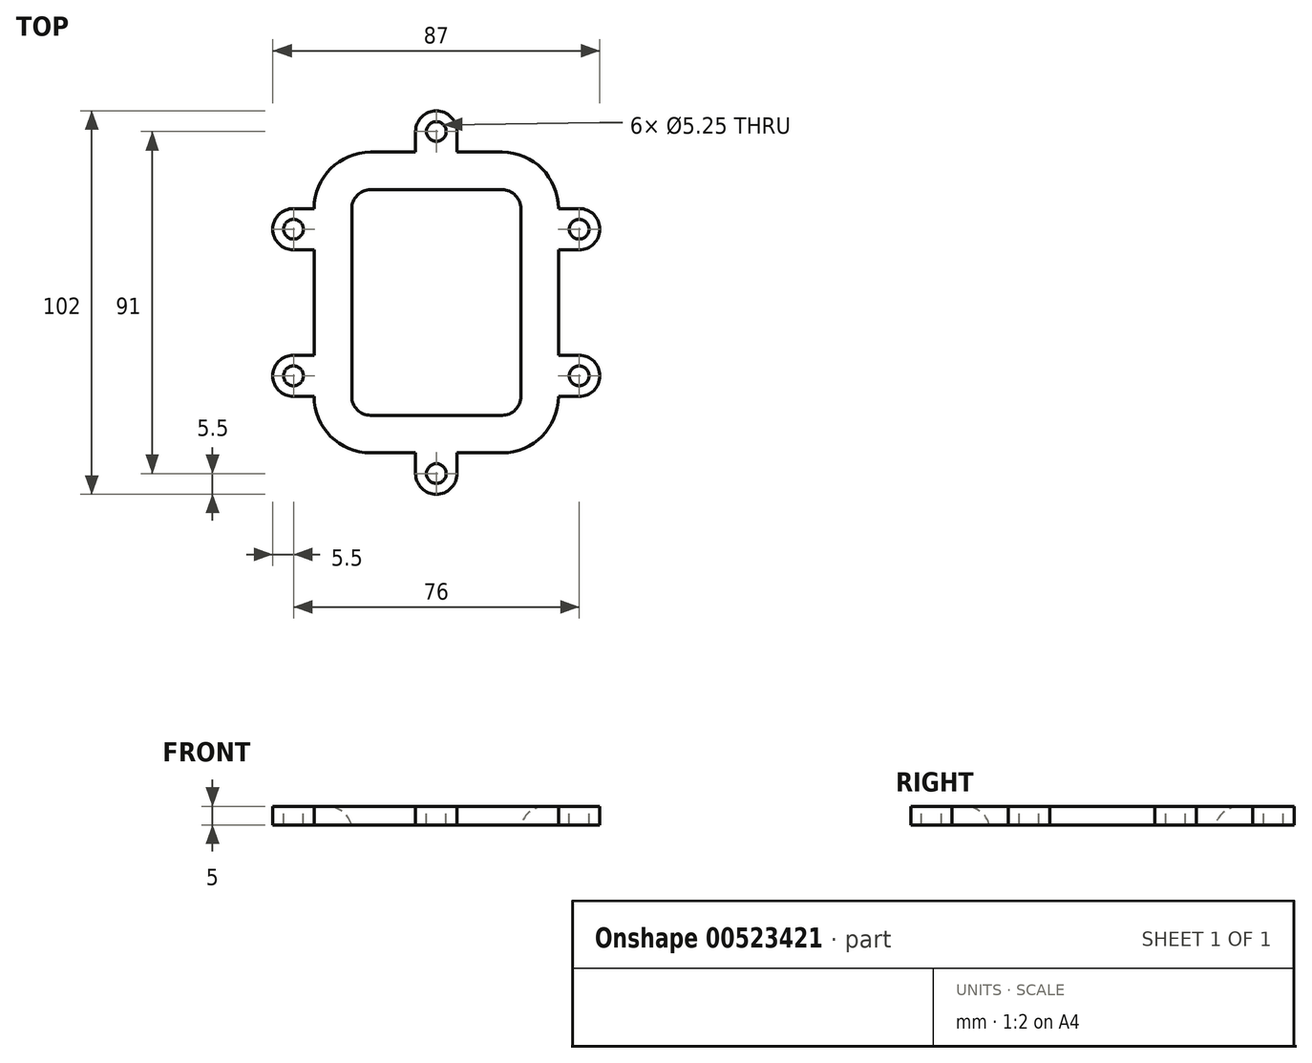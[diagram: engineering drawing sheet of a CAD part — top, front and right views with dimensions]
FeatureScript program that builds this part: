
annotation { "Feature Type Name" : "Feature", "Feature Type Description" : "" }
export const myFeature = defineFeature(function(context is Context, id is Id, definition is map)
    precondition{}
    {
        {
            var Q0;
            Q0=qCreatedBy(makeId("Top.planeOp"),FACE);
            var sketch = newSketch(context, id + "F0", { "sketchPlane" : qUnion([Q0])});
            skLineSegment(sketch, "E0.bottom", {"start": v(-17.5, -30) * mm, "end": v(17.5, -30) * mm});
            skLineSegment(sketch, "E0.top", {"start": v(-17.5, 30) * mm, "end": v(17.5, 30) * mm});
            skLineSegment(sketch, "E0.left", {"start": v(-22.5, -25) * mm, "end": v(-22.5, 25) * mm});
            skLineSegment(sketch, "E0.right", {"start": v(22.5, -25) * mm, "end": v(22.5, 25) * mm});
            skPoint(sketch, "E0.middle", {"position": v(0, 0) * mm});
            skPoint(sketch, "E1.visualSharp", {"position": v(22.5, -30) * mm});
            skArc(sketch, "E1.filletArc", {"start": v(17.5, -30) * mm, "mid": v(21.04, -28.54) * mm, "end": v(22.5, -25) * mm});
            skPoint(sketch, "E2.visualSharp", {"position": v(-22.5, -30) * mm});
            skArc(sketch, "E2.filletArc", {"start": v(-22.5, -25) * mm, "mid": v(-21.04, -28.54) * mm, "end": v(-17.5, -30) * mm});
            skPoint(sketch, "E3.visualSharp", {"position": v(-22.5, 30) * mm});
            skArc(sketch, "E3.filletArc", {"start": v(-17.5, 30) * mm, "mid": v(-21.04, 28.54) * mm, "end": v(-22.5, 25) * mm});
            skPoint(sketch, "E4.visualSharp", {"position": v(22.5, 30) * mm});
            skArc(sketch, "E4.filletArc", {"start": v(22.5, 25) * mm, "mid": v(21.04, 28.54) * mm, "end": v(17.5, 30) * mm});
            skArc(sketch, "E5.0", {"start": v(-32.5, -25) * mm, "mid": v(-28.1, -35.6) * mm, "end": v(-17.5, -40) * mm});
            skLineSegment(sketch, "E5.1", {"start": v(-17.5, -40) * mm, "end": v(-5.5, -40) * mm});
            skLineSegment(sketch, "E5.2", {"start": v(-32.5, -14) * mm, "end": v(-32.5, 14) * mm});
            skArc(sketch, "E5.3", {"start": v(17.5, -40) * mm, "mid": v(28.1, -35.6) * mm, "end": v(32.5, -25) * mm});
            skArc(sketch, "E5.4", {"start": v(-17.5, 40) * mm, "mid": v(-28.1, 35.6) * mm, "end": v(-32.5, 25) * mm});
            skLineSegment(sketch, "E5.5", {"start": v(-17.5, 40) * mm, "end": v(-5.5, 40) * mm});
            skArc(sketch, "E5.6", {"start": v(32.5, 25) * mm, "mid": v(28.1, 35.6) * mm, "end": v(17.5, 40) * mm});
            skLineSegment(sketch, "E5.7", {"start": v(32.5, -14) * mm, "end": v(32.5, 14) * mm});
            skArc(sketch, "E6", {"start": v(-38, 25) * mm, "mid": v(-43.5, 19.5) * mm, "end": v(-38, 14) * mm});
            skLineSegment(sketch, "E7", {"start": v(-38, 25) * mm, "end": v(-32.5, 25) * mm});
            skLineSegment(sketch, "E8", {"start": v(-38, 14) * mm, "end": v(-32.5, 14) * mm});
            skCircle(sketch, "E9", {"center": v(-38, 19.5) * mm, "radius": 2.5 * mm, "construction": true});
            skLineSegment(sketch, "E10", {"start": v(0, 49.94) * mm, "end": v(0, -61.1) * mm, "construction": true});
            skLineSegment(sketch, "E11", {"start": v(-88.08, 0) * mm, "end": v(87.86, 0) * mm, "construction": true});
            skLineSegment(sketch, "E12.MirrorCS", {"start": v(38, 25) * mm, "end": v(32.5, 25) * mm});
            skLineSegment(sketch, "E13.MirrorCS", {"start": v(38, 14) * mm, "end": v(32.5, 14) * mm});
            skArc(sketch, "E14.MirrorCS", {"start": v(38, 25) * mm, "mid": v(43.5, 19.5) * mm, "end": v(38, 14) * mm});
            skCircle(sketch, "E15.MirrorC", {"center": v(38, 19.5) * mm, "radius": 2.5 * mm, "construction": true});
            skLineSegment(sketch, "E16.MirrorCS", {"start": v(-38, -14) * mm, "end": v(-32.5, -14) * mm});
            skLineSegment(sketch, "E17.MirrorCS", {"start": v(-38, -25) * mm, "end": v(-32.5, -25) * mm});
            skArc(sketch, "E18.MirrorCS", {"start": v(-38, -25) * mm, "mid": v(-43.5, -19.5) * mm, "end": v(-38, -14) * mm});
            skCircle(sketch, "E19.MirrorC", {"center": v(-38, -19.5) * mm, "radius": 2.5 * mm, "construction": true});
            skArc(sketch, "E20.MirrorCS", {"start": v(32.5, -25) * mm, "mid": v(28.1, -35.6) * mm, "end": v(17.5, -40) * mm});
            skLineSegment(sketch, "E21.MirrorCS", {"start": v(38, -14) * mm, "end": v(32.5, -14) * mm});
            skArc(sketch, "E22.MirrorCS", {"start": v(38, -25) * mm, "mid": v(43.5, -19.5) * mm, "end": v(38, -14) * mm});
            skLineSegment(sketch, "E23.MirrorCS", {"start": v(32.5, 14) * mm, "end": v(32.5, -14) * mm});
            skCircle(sketch, "E24.MirrorC", {"center": v(38, -19.5) * mm, "radius": 2.5 * mm, "construction": true});
            skLineSegment(sketch, "E25.MirrorCS", {"start": v(38, -25) * mm, "end": v(32.5, -25) * mm});
            skPoint(sketch, "E26.orphan", {"position": v(32.5, 25) * mm});
            skArc(sketch, "E27", {"start": v(5.5, 45.5) * mm, "mid": v(0, 51) * mm, "end": v(-5.5, 45.5) * mm});
            skCircle(sketch, "E28", {"center": v(0, 45.5) * mm, "radius": 2.5 * mm, "construction": true});
            skLineSegment(sketch, "E29", {"start": v(5.5, 45.5) * mm, "end": v(5.5, 40) * mm});
            skLineSegment(sketch, "E30", {"start": v(-5.5, 45.5) * mm, "end": v(-5.5, 40) * mm});
            skLineSegment(sketch, "E31.trimOffspring", {"start": v(5.5, 40) * mm, "end": v(17.5, 40) * mm});
            skArc(sketch, "E32.MirrorCS", {"start": v(5.5, -45.5) * mm, "mid": v(0, -51) * mm, "end": v(-5.5, -45.5) * mm});
            skCircle(sketch, "E33.MirrorC", {"center": v(0, -45.5) * mm, "radius": 2.5 * mm, "construction": true});
            skLineSegment(sketch, "E34.MirrorCS", {"start": v(5.5, -45.5) * mm, "end": v(5.5, -40) * mm});
            skLineSegment(sketch, "E35.MirrorCS", {"start": v(-5.5, -45.5) * mm, "end": v(-5.5, -40) * mm});
            skLineSegment(sketch, "E36.trimOffspring", {"start": v(5.5, -40) * mm, "end": v(17.5, -40) * mm});
            skSolve(sketch);
        }
        {
            var Q0;
            Q0=qSketchRegion(id+"F0",true);
            extrude(context, id + "F1", {"entities" : qUnion([Q0]), "depth" : 5 * mm, "offsetDistance" : 25 * mm});
        }
        {
            var Q0;
            {var subQ0=sQuery(id+"F0.wireOp",EDGE,"E25.MirrorCS");var subQ1=sQuery(id+"F0.wireOp",EDGE,"E23.MirrorCS");var subQ2=sQuery(id+"F0.wireOp",EDGE,"E22.MirrorCS");var subQ3=sQuery(id+"F0.wireOp",EDGE,"E21.MirrorCS");var subQ4=sQuery(id+"F0.wireOp",EDGE,"E20.MirrorCS");var subQ5=sQuery(id+"F0.wireOp",EDGE,"E18.MirrorCS");var subQ6=sQuery(id+"F0.wireOp",EDGE,"E17.MirrorCS");var subQ7=sQuery(id+"F0.wireOp",EDGE,"E16.MirrorCS");var subQ8=sQuery(id+"F0.wireOp",EDGE,"E14.MirrorCS");var subQ9=sQuery(id+"F0.wireOp",EDGE,"E13.MirrorCS");var subQ10=sQuery(id+"F0.wireOp",EDGE,"E5.4");var subQ11=sQuery(id+"F0.wireOp",EDGE,"E5.2");var subQ12=sQuery(id+"F0.wireOp",EDGE,"E5.1");var subQ13=sQuery(id+"F0.wireOp",EDGE,"E5.0");var subQ14=sQuery(id+"F0.wireOp",EDGE,"E5.5");var subQ15=sQuery(id+"F0.wireOp",EDGE,"E5.6");var subQ16=sQuery(id+"F0.wireOp",EDGE,"E6");var subQ17=sQuery(id+"F0.wireOp",EDGE,"E7");var subQ18=sQuery(id+"F0.wireOp",EDGE,"E8");var subQ19=sQuery(id+"F0.wireOp",EDGE,"E12.MirrorCS");Q0=makeQuery(id+"Fk4e8jRBaSHLmWu_1.boolean.opBoolean","SPLIT",FACE,{"disambiguationData":[TD([makeQuery(id+"F1.opExtrude","SWEPT_FACE",FACE,{"disambiguationData":[OSD([subQ13])]})])],"derivedFrom":makeQuery(id+"F1.opExtrude","CAP_FACE",FACE,{"disambiguationData":[OSD([sQuery(id+"F0.wireOp",EDGE,"E0.bottom"),sQuery(id+"F0.wireOp",EDGE,"E0.top"),sQuery(id+"F0.wireOp",EDGE,"E0.left"),sQuery(id+"F0.wireOp",EDGE,"E0.right"),sQuery(id+"F0.wireOp",EDGE,"E1.filletArc"),sQuery(id+"F0.wireOp",EDGE,"E2.filletArc"),sQuery(id+"F0.wireOp",EDGE,"E3.filletArc"),sQuery(id+"F0.wireOp",EDGE,"E4.filletArc"),subQ13,subQ12,subQ11,subQ10,subQ14,subQ15,subQ16,subQ17,subQ18,subQ19,subQ9,subQ8,subQ7,subQ6,subQ5,subQ4,subQ3,subQ2,subQ1,subQ0])],"isStart":false})});}
            var sketch = newSketch(context, id + "F2", { "sketchPlane" : qUnion([Q0])});
            skPoint(sketch, "E37", {"position": v(-38, 19.5) * mm});
            skPoint(sketch, "E38", {"position": v(0, 45.5) * mm});
            skPoint(sketch, "E39", {"position": v(38, 19.5) * mm});
            skPoint(sketch, "E40", {"position": v(38, -19.5) * mm});
            skPoint(sketch, "E41", {"position": v(0, -45.5) * mm});
            skPoint(sketch, "E42", {"position": v(-38, -19.5) * mm});
            skSolve(sketch);
        }
        {
            var Q0;
            Q0=sQuery(id+"F2.wireOp",VERTEX,"E37");
            var Q1;
            Q1=sQuery(id+"F2.wireOp",VERTEX,"E38");
            var Q2;
            Q2=sQuery(id+"F2.wireOp",VERTEX,"E39");
            var Q3;
            Q3=sQuery(id+"F2.wireOp",VERTEX,"E40");
            var Q4;
            Q4=sQuery(id+"F2.wireOp",VERTEX,"E41");
            var Q5;
            Q5=sQuery(id+"F2.wireOp",VERTEX,"E42");
            var Q6;
            Q6=makeQuery(id+"F1.opExtrude","SWEPT_BODY",BODY,{"disambiguationData":[OSD([sQuery(id+"F0.wireOp",EDGE,"E0.bottom"),sQuery(id+"F0.wireOp",EDGE,"E0.top"),sQuery(id+"F0.wireOp",EDGE,"E0.left"),sQuery(id+"F0.wireOp",EDGE,"E0.right"),sQuery(id+"F0.wireOp",EDGE,"E1.filletArc"),sQuery(id+"F0.wireOp",EDGE,"E2.filletArc"),sQuery(id+"F0.wireOp",EDGE,"E3.filletArc"),sQuery(id+"F0.wireOp",EDGE,"E4.filletArc"),sQuery(id+"F0.wireOp",EDGE,"E5.0"),sQuery(id+"F0.wireOp",EDGE,"E5.1"),sQuery(id+"F0.wireOp",EDGE,"E5.2"),sQuery(id+"F0.wireOp",EDGE,"E5.4"),sQuery(id+"F0.wireOp",EDGE,"E5.5"),sQuery(id+"F0.wireOp",EDGE,"E5.6"),sQuery(id+"F0.wireOp",EDGE,"E6"),sQuery(id+"F0.wireOp",EDGE,"E7"),sQuery(id+"F0.wireOp",EDGE,"E8"),sQuery(id+"F0.wireOp",EDGE,"E12.MirrorCS"),sQuery(id+"F0.wireOp",EDGE,"E13.MirrorCS"),sQuery(id+"F0.wireOp",EDGE,"E14.MirrorCS"),sQuery(id+"F0.wireOp",EDGE,"E16.MirrorCS"),sQuery(id+"F0.wireOp",EDGE,"E17.MirrorCS"),sQuery(id+"F0.wireOp",EDGE,"E18.MirrorCS"),sQuery(id+"F0.wireOp",EDGE,"E20.MirrorCS"),sQuery(id+"F0.wireOp",EDGE,"E21.MirrorCS"),sQuery(id+"F0.wireOp",EDGE,"E22.MirrorCS"),sQuery(id+"F0.wireOp",EDGE,"E23.MirrorCS"),sQuery(id+"F0.wireOp",EDGE,"E25.MirrorCS"),sQuery(id+"F0.wireOp",EDGE,"E27"),sQuery(id+"F0.wireOp",EDGE,"E29"),sQuery(id+"F0.wireOp",EDGE,"E30"),sQuery(id+"F0.wireOp",EDGE,"E31.trimOffspring"),sQuery(id+"F0.wireOp",EDGE,"E32.MirrorCS"),sQuery(id+"F0.wireOp",EDGE,"E34.MirrorCS"),sQuery(id+"F0.wireOp",EDGE,"E35.MirrorCS"),sQuery(id+"F0.wireOp",EDGE,"E36.trimOffspring")])]});
            hole(context, id + "F3", {"style" : HoleStyle.SIMPLE, "endStyle" : HoleEndStyle.BLIND, "standardTappedOrClearance" : lookupTablePath({ "standard" : "ISO", "fit" : "Close", "size" : "M5", "type" : "Clearance" }), "standardBlindInLast" : lookupTablePath({ "fit" : "Close", "standard" : "ISO", "size" : "M5", "type" : "Clearance" }), "holeDiameter" : 5.25 * mm, "holeDepth" : 40 * mm, "isTappedThrough" : true, "tappedDepth" : 37.6 * mm, "tapClearance" : 3, "locations" : qUnion([Q0, Q1, Q2, Q3, Q4, Q5]), "scope" : qUnion([Q6])});
        }
        {
            var Q0;
            Q0=makeQuery(id+"F1.opExtrude","CAP_EDGE",EDGE,{"disambiguationData":[OSD([sQuery(id+"F0.wireOp",EDGE,"E0.left")])],"isStart":false});
            fillet(context, id + "F4", {"entities" : qUnion([Q0]), "radius" : 7 * mm, "tangentPropagation" : true, "allowEdgeOverflow" : false});
        }
    });
